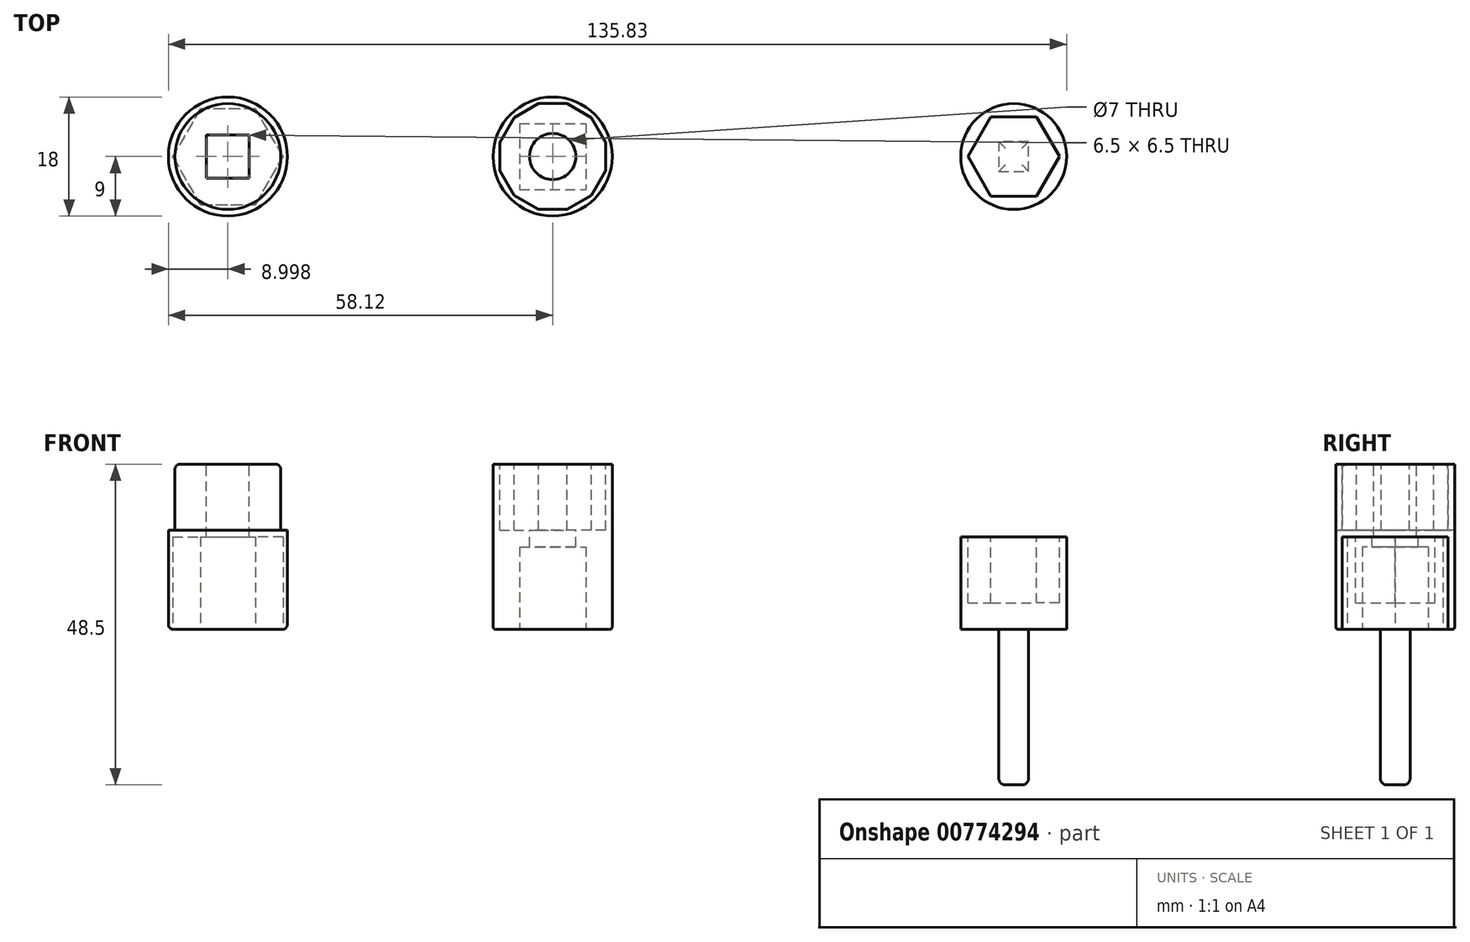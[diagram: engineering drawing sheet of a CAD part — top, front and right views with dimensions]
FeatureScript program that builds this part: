
annotation { "Feature Type Name" : "Feature", "Feature Type Description" : "" }
export const myFeature = defineFeature(function(context is Context, id is Id, definition is map)
    precondition{}
    {
        {
            var Q0;
            Q0=qCreatedBy(makeId("Top.planeOp"),FACE);
            var sketch = newSketch(context, id + "F0", { "sketchPlane" : qUnion([Q0])});
            skCircle(sketch, "E0", {"center": v(0, 0) * mm, "radius": 9 * mm});
            skLineSegment(sketch, "E1.bottom", {"start": v(-5, 5) * mm, "end": v(5, 5) * mm});
            skLineSegment(sketch, "E1.top", {"start": v(-5, -5) * mm, "end": v(5, -5) * mm});
            skLineSegment(sketch, "E1.left", {"start": v(-5, 5) * mm, "end": v(-5, -5) * mm});
            skLineSegment(sketch, "E1.right", {"start": v(5, 5) * mm, "end": v(5, -5) * mm});
            skSolve(sketch);
        }
        {
            var Q0;
            Q0=makeQuery(id+"F0.imprint","IMPRINT",FACE,{"disambiguationData":[TD([[makeQuery(id+"F0.imprint","IMPRINT",EDGE,{"derivedFrom":sQuery(id+"F0.wireOp",EDGE,"E0")}),1.0]])]});
            var Q1;
            {var subQ1=sQuery(id+"F0.wireOp",EDGE,"03wSvE2e-Fg7S-AAcF-NH9x-LQPhPzigft5H.right");var subQ6=sQuery(id+"F0.wireOp",EDGE,"03wSvE2e-Fg7S-AAcF-NH9x-LQPhPzigft5H.bottom");var subQ9=makeQuery(id+"F0.imprint","INTERSECT",VERTEX,{"derivedFrom":[subQ6,subQ1]});Q1=makeQuery(id+"F0.imprint","IMPRINT",FACE,{"disambiguationData":[TD([[makeQuery(id+"F0.imprint","IMPRINT",EDGE,{"disambiguationData":[TD([[subQ9,1.0]])],"derivedFrom":subQ6}),-1.0]])]});}
            var Q2;
            {var subQ1=sQuery(id+"F0.wireOp",EDGE,"03wSvE2e-Fg7S-AAcF-NH9x-LQPhPzigft5H.right");var subQ6=sQuery(id+"F0.wireOp",EDGE,"03wSvE2e-Fg7S-AAcF-NH9x-LQPhPzigft5H.top");var subQ9=makeQuery(id+"F0.imprint","INTERSECT",VERTEX,{"derivedFrom":[subQ6,subQ1]});Q2=makeQuery(id+"F0.imprint","IMPRINT",FACE,{"disambiguationData":[TD([[makeQuery(id+"F0.imprint","IMPRINT",EDGE,{"disambiguationData":[TD([[subQ9,1.0]])],"derivedFrom":subQ6}),1.0]])]});}
            var Q3;
            {var subQ1=sQuery(id+"F0.wireOp",EDGE,"03wSvE2e-Fg7S-AAcF-NH9x-LQPhPzigft5H.top");var subQ5=sQuery(id+"F0.wireOp",EDGE,"03wSvE2e-Fg7S-AAcF-NH9x-LQPhPzigft5H.left");var subQ6=makeQuery(id+"F0.imprint","INTERSECT",VERTEX,{"derivedFrom":[subQ1,subQ5]});Q3=makeQuery(id+"F0.imprint","IMPRINT",FACE,{"disambiguationData":[TD([[makeQuery(id+"F0.imprint","IMPRINT",EDGE,{"disambiguationData":[TD([[subQ6,-1.0]])],"derivedFrom":subQ1}),1.0]])]});}
            var Q4;
            {var subQ1=sQuery(id+"F0.wireOp",EDGE,"03wSvE2e-Fg7S-AAcF-NH9x-LQPhPzigft5H.left");var subQ6=sQuery(id+"F0.wireOp",EDGE,"03wSvE2e-Fg7S-AAcF-NH9x-LQPhPzigft5H.bottom");var subQ9=makeQuery(id+"F0.imprint","INTERSECT",VERTEX,{"derivedFrom":[subQ6,subQ1]});Q4=makeQuery(id+"F0.imprint","IMPRINT",FACE,{"disambiguationData":[TD([[makeQuery(id+"F0.imprint","IMPRINT",EDGE,{"disambiguationData":[TD([[subQ9,-1.0]])],"derivedFrom":subQ6}),-1.0]])]});}
            var Q5;
            {var subQ0=sQuery(id+"F0.wireOp",EDGE,"0nZERG67-7UOP-U3bg-9f60-7EF7LwZAKck1");var subQ1=sQuery(id+"F0.wireOp",EDGE,"W0zUS9TI-iheG-UtfQ-mQPj-YblpC81evcvk");var subQ2=makeQuery(id+"F0.imprint","INTERSECT",VERTEX,{"disambiguationData":[OD(0.0)],"derivedFrom":[subQ1,subQ0]});Q5=makeQuery(id+"F0.imprint","IMPRINT",FACE,{"disambiguationData":[TD([[makeQuery(id+"F0.imprint","IMPRINT",EDGE,{"disambiguationData":[TD([[subQ2,-1.0]])],"derivedFrom":subQ1}),-1.0]])]});}
            var Q6;
            {var subQ0=sQuery(id+"F0.wireOp",EDGE,"zQuLa7GF-zexE-TRTW-qUjA-5ZPmynHRBfk2");var subQ1=sQuery(id+"F0.wireOp",EDGE,"W0zUS9TI-iheG-UtfQ-mQPj-YblpC81evcvk");var subQ2=makeQuery(id+"F0.imprint","INTERSECT",VERTEX,{"derivedFrom":[subQ1,subQ0]});Q6=makeQuery(id+"F0.imprint","IMPRINT",FACE,{"disambiguationData":[TD([[makeQuery(id+"F0.imprint","IMPRINT",EDGE,{"disambiguationData":[TD([[subQ2,-1.0]])],"derivedFrom":subQ1}),1.0]])]});}
            var Q7;
            {var subQ0=sQuery(id+"F0.wireOp",EDGE,"zQuLa7GF-zexE-TRTW-qUjA-5ZPmynHRBfk2");var subQ1=sQuery(id+"F0.wireOp",EDGE,"W0zUS9TI-iheG-UtfQ-mQPj-YblpC81evcvk");var subQ2=makeQuery(id+"F0.imprint","INTERSECT",VERTEX,{"derivedFrom":[subQ1,subQ0]});Q7=makeQuery(id+"F0.imprint","IMPRINT",FACE,{"disambiguationData":[TD([[makeQuery(id+"F0.imprint","IMPRINT",EDGE,{"disambiguationData":[TD([[subQ2,-1.0]])],"derivedFrom":subQ1}),-1.0]])]});}
            var Q8;
            {var subQ0=sQuery(id+"F0.wireOp",EDGE,"0nZERG67-7UOP-U3bg-9f60-7EF7LwZAKck1");var subQ1=sQuery(id+"F0.wireOp",EDGE,"W0zUS9TI-iheG-UtfQ-mQPj-YblpC81evcvk");var subQ2=makeQuery(id+"F0.imprint","INTERSECT",VERTEX,{"disambiguationData":[OD(0.0)],"derivedFrom":[subQ1,subQ0]});Q8=makeQuery(id+"F0.imprint","IMPRINT",FACE,{"disambiguationData":[TD([[makeQuery(id+"F0.imprint","IMPRINT",EDGE,{"disambiguationData":[TD([[subQ2,-1.0]])],"derivedFrom":subQ1}),1.0]])]});}
            extrude(context, id + "F1", {"entities" : qUnion([Q0, Q1, Q2, Q3, Q4, Q5, Q6, Q7, Q8]), "depth" : 12.5 * mm, "offsetDistance" : 25 * mm});
        }
        {
            var Q0;
            Q0=makeQuery(id+"F1.opExtrude","CAP_EDGE",EDGE,{"disambiguationData":[OSD([sQuery(id+"F0.wireOp",EDGE,"E0")])],"isStart":true});
            fillet(context, id + "F2", {"entities" : qUnion([Q0]), "radius" : .4 * mm, "tangentPropagation" : true, "allowEdgeOverflow" : false});
        }
        {
            var Q0;
            Q0=makeQuery(id+"F1.opExtrude","CAP_FACE",FACE,{"disambiguationData":[OSD([sQuery(id+"F0.wireOp",EDGE,"E0")])],"isStart":false});
            var sketch = newSketch(context, id + "F3", { "sketchPlane" : qUnion([Q0])});
            skCircle(sketch, "E2", {"center": v(0, 0) * mm, "radius": 9 * mm});
            skSolve(sketch);
        }
        {
            var Q0;
            Q0 = qSketchRegion(id + "F3", true);
            extrude(context, id + "F4", {"entities" : qUnion([Q0]), "operationType" : NewBodyOperationType.ADD, "depth" : 12.5 * mm, "offsetDistance" : 25 * mm});
        }
        {
            var Q0;
            Q0=makeQuery(id+"F4.opExtrude","CAP_FACE",FACE,{"disambiguationData":[OSD([sQuery(id+"F3.wireOp",EDGE,"E2")])],"isStart":false});
            var sketch = newSketch(context, id + "F5", { "sketchPlane" : qUnion([Q0])});
            skCircle(sketch, "E3.cCircle", {"center": v(0, 0) * mm, "radius": 8 * mm, "construction": true});
            skLineSegment(sketch, "E3.0", {"start": v(-2.14, 8) * mm, "end": v(2.14, 8) * mm});
            skLineSegment(sketch, "E3.1", {"start": v(2.14, 8) * mm, "end": v(5.86, 5.86) * mm});
            skLineSegment(sketch, "E3.2", {"start": v(5.86, 5.86) * mm, "end": v(8, 2.14) * mm});
            skLineSegment(sketch, "E3.3", {"start": v(8, 2.14) * mm, "end": v(8, -2.14) * mm});
            skLineSegment(sketch, "E3.4", {"start": v(8, -2.14) * mm, "end": v(5.86, -5.86) * mm});
            skLineSegment(sketch, "E3.5", {"start": v(5.86, -5.86) * mm, "end": v(2.14, -8) * mm});
            skLineSegment(sketch, "E3.6", {"start": v(2.14, -8) * mm, "end": v(-2.14, -8) * mm});
            skLineSegment(sketch, "E3.7", {"start": v(-2.14, -8) * mm, "end": v(-5.86, -5.86) * mm});
            skLineSegment(sketch, "E3.8", {"start": v(-5.86, -5.86) * mm, "end": v(-8, -2.14) * mm});
            skLineSegment(sketch, "E3.9", {"start": v(-8, -2.14) * mm, "end": v(-8, 2.14) * mm});
            skLineSegment(sketch, "E3.10", {"start": v(-8, 2.14) * mm, "end": v(-5.86, 5.86) * mm});
            skLineSegment(sketch, "E3.11", {"start": v(-5.86, 5.86) * mm, "end": v(-2.14, 8) * mm});
            skPoint(sketch, "E3.0.midPoint", {"position": v(0, 8) * mm});
            skSolve(sketch);
        }
        {
            var Q0;
            Q0 = qSketchRegion(id + "F5", true);
            extrude(context, id + "F6", {"entities" : qUnion([Q0]), "operationType" : NewBodyOperationType.REMOVE, "oppositeDirection" : true, "depth" : 10 * mm, "offsetDistance" : 25 * mm});
        }
        {
            var Q0;
            Q0=qCreatedBy(makeId("Top.planeOp"),FACE);
            var sketch = newSketch(context, id + "F7", { "sketchPlane" : qUnion([Q0])});
            skCircle(sketch, "E4", {"center": v(69.71, 0) * mm, "radius": 8 * mm});
            skSolve(sketch);
        }
        {
            var Q0;
            Q0 = qSketchRegion(id + "F7", true);
            extrude(context, id + "F8", {"entities" : qUnion([Q0]), "depth" : 14 * mm, "offsetDistance" : 25 * mm});
        }
        {
            var Q0;
            Q0=makeQuery(id+"F8.opExtrude","CAP_FACE",FACE,{"disambiguationData":[OSD([sQuery(id+"F7.wireOp",EDGE,"E4")])],"isStart":true});
            var sketch = newSketch(context, id + "F9", { "sketchPlane" : qUnion([Q0])});
            skCircle(sketch, "E5.cCircle", {"center": v(69.71, 0) * mm, "radius": 2.25 * mm});
            skLineSegment(sketch, "E5.0", {"start": v(67.46, 2.25) * mm, "end": v(71.96, 2.25) * mm});
            skLineSegment(sketch, "E5.1", {"start": v(71.96, 2.25) * mm, "end": v(71.96, -2.25) * mm});
            skLineSegment(sketch, "E5.2", {"start": v(71.96, -2.25) * mm, "end": v(67.46, -2.25) * mm});
            skLineSegment(sketch, "E5.3", {"start": v(67.46, -2.25) * mm, "end": v(67.46, 2.25) * mm});
            skPoint(sketch, "E5.0.midPoint", {"position": v(69.71, 2.25) * mm});
            skSolve(sketch);
        }
        {
            var Q0;
            {var subQ0=sQuery(id+"F9.wireOp",EDGE,"E5.1");var subQ1=sQuery(id+"F9.wireOp",EDGE,"E5.cCircle");var subQ2=makeQuery(id+"F9.imprint","INTERSECT",VERTEX,{"derivedFrom":[subQ1,subQ0]});Q0=makeQuery(id+"F9.imprint","IMPRINT",FACE,{"disambiguationData":[TD([[makeQuery(id+"F9.imprint","IMPRINT",EDGE,{"disambiguationData":[TD([[subQ2,1.0]])],"derivedFrom":subQ1}),-1.0]])]});}
            var Q1;
            {var subQ0=sQuery(id+"F9.wireOp",EDGE,"E5.0");var subQ1=sQuery(id+"F9.wireOp",EDGE,"E5.cCircle");var subQ2=makeQuery(id+"F9.imprint","INTERSECT",VERTEX,{"derivedFrom":[subQ1,subQ0]});Q1=makeQuery(id+"F9.imprint","IMPRINT",FACE,{"disambiguationData":[TD([[makeQuery(id+"F9.imprint","IMPRINT",EDGE,{"disambiguationData":[TD([[subQ2,1.0]])],"derivedFrom":subQ1}),-1.0]])]});}
            var Q2;
            {var subQ0=sQuery(id+"F9.wireOp",EDGE,"E5.3");var subQ1=sQuery(id+"F9.wireOp",EDGE,"E5.cCircle");var subQ2=makeQuery(id+"F9.imprint","INTERSECT",VERTEX,{"derivedFrom":[subQ1,subQ0]});Q2=makeQuery(id+"F9.imprint","IMPRINT",FACE,{"disambiguationData":[TD([[makeQuery(id+"F9.imprint","IMPRINT",EDGE,{"disambiguationData":[TD([[subQ2,-1.0]])],"derivedFrom":subQ1}),-1.0]])]});}
            var Q3;
            {var subQ0=sQuery(id+"F9.wireOp",EDGE,"E5.cCircle");var subQ1=makeQuery(id+"F9.imprint","INTERSECT",VERTEX,{"derivedFrom":[subQ0,sQuery(id+"F9.wireOp",EDGE,"E5.0")]});Q3=makeQuery(id+"F9.imprint","IMPRINT",FACE,{"disambiguationData":[TD([[makeQuery(id+"F9.imprint","IMPRINT",EDGE,{"disambiguationData":[TD([[subQ1,1.0]])],"derivedFrom":subQ0}),1.0]])]});}
            var Q4;
            {var subQ0=sQuery(id+"F9.wireOp",EDGE,"E5.0");var subQ1=sQuery(id+"F9.wireOp",EDGE,"E5.cCircle");var subQ2=makeQuery(id+"F9.imprint","INTERSECT",VERTEX,{"derivedFrom":[subQ1,subQ0]});Q4=makeQuery(id+"F9.imprint","IMPRINT",FACE,{"disambiguationData":[TD([[makeQuery(id+"F9.imprint","IMPRINT",EDGE,{"disambiguationData":[TD([[subQ2,-1.0]])],"derivedFrom":subQ1}),-1.0]])]});}
            extrude(context, id + "F10", {"entities" : qUnion([Q0, Q1, Q2, Q3, Q4]), "operationType" : NewBodyOperationType.ADD, "depth" : 23.5 * mm, "offsetDistance" : 25 * mm});
        }
        {
            var Q0;
            Q0=makeQuery(id+"F6.boolean.opBoolean","COPY",FACE,{"derivedFrom":makeQuery(id+"F6.opExtrude","CAP_FACE",FACE,{"disambiguationData":[OSD([sQuery(id+"F5.wireOp",EDGE,"E3.0"),sQuery(id+"F5.wireOp",EDGE,"E3.1"),sQuery(id+"F5.wireOp",EDGE,"E3.2"),sQuery(id+"F5.wireOp",EDGE,"E3.3"),sQuery(id+"F5.wireOp",EDGE,"E3.4"),sQuery(id+"F5.wireOp",EDGE,"E3.5"),sQuery(id+"F5.wireOp",EDGE,"E3.6"),sQuery(id+"F5.wireOp",EDGE,"E3.7"),sQuery(id+"F5.wireOp",EDGE,"E3.8"),sQuery(id+"F5.wireOp",EDGE,"E3.9"),sQuery(id+"F5.wireOp",EDGE,"E3.10"),sQuery(id+"F5.wireOp",EDGE,"E3.11")])],"isStart":false})});
            var sketch = newSketch(context, id + "F11", { "sketchPlane" : qUnion([Q0])});
            skCircle(sketch, "E6", {"center": v(0, 0) * mm, "radius": 3.5 * mm});
            skSolve(sketch);
        }
        {
            var Q0;
            Q0 = qSketchRegion(id + "F11", true);
            extrude(context, id + "F12", {"entities" : qUnion([Q0]), "operationType" : NewBodyOperationType.REMOVE, "oppositeDirection" : true, "depth" : 12 * mm, "offsetDistance" : 25 * mm});
        }
        {
            var Q0;
            Q0=makeQuery(id+"F10.opExtrude","CAP_EDGE",EDGE,{"disambiguationData":[OSD([sQuery(id+"F9.wireOp",EDGE,"E5.2")])],"isStart":false});
            var Q1;
            Q1=makeQuery(id+"F10.opExtrude","CAP_EDGE",EDGE,{"disambiguationData":[OSD([sQuery(id+"F9.wireOp",EDGE,"E5.1")])],"isStart":false});
            var Q2;
            Q2=makeQuery(id+"F10.opExtrude","CAP_EDGE",EDGE,{"disambiguationData":[OSD([sQuery(id+"F9.wireOp",EDGE,"E5.0")])],"isStart":false});
            var Q3;
            Q3=makeQuery(id+"F10.opExtrude","CAP_EDGE",EDGE,{"disambiguationData":[OSD([sQuery(id+"F9.wireOp",EDGE,"E5.3")])],"isStart":false});
            fillet(context, id + "F13", {"entities" : qUnion([Q0, Q1, Q2, Q3]), "radius" : 1 * mm, "tangentPropagation" : true, "allowEdgeOverflow" : false});
        }
        {
            var Q0;
            Q0=qCreatedBy(makeId("Top.planeOp"),FACE);
            var sketch = newSketch(context, id + "F14", { "sketchPlane" : qUnion([Q0])});
            skCircle(sketch, "E7", {"center": v(-49.12, 0) * mm, "radius": 9 * mm});
            skSolve(sketch);
        }
        {
            var Q0;
            Q0 = qSketchRegion(id + "F14", true);
            extrude(context, id + "F15", {"entities" : qUnion([Q0]), "depth" : 15 * mm, "offsetDistance" : 25 * mm});
        }
        {
            var Q0;
            Q0=makeQuery(id+"F15.opExtrude","CAP_FACE",FACE,{"disambiguationData":[OSD([sQuery(id+"F14.wireOp",EDGE,"E7"),sQuery(id+"F14.wireOp",EDGE,"6d6a7b4d-6cfd-47b6-aa00-b523f6408a61.0"),sQuery(id+"F14.wireOp",EDGE,"6d6a7b4d-6cfd-47b6-aa00-b523f6408a61.1"),sQuery(id+"F14.wireOp",EDGE,"6d6a7b4d-6cfd-47b6-aa00-b523f6408a61.2"),sQuery(id+"F14.wireOp",EDGE,"6d6a7b4d-6cfd-47b6-aa00-b523f6408a61.3"),sQuery(id+"F14.wireOp",EDGE,"6d6a7b4d-6cfd-47b6-aa00-b523f6408a61.4"),sQuery(id+"F14.wireOp",EDGE,"6d6a7b4d-6cfd-47b6-aa00-b523f6408a61.5")])],"isStart":false});
            var sketch = newSketch(context, id + "F16", { "sketchPlane" : qUnion([Q0])});
            skCircle(sketch, "E8", {"center": v(-49.12, 0) * mm, "radius": 8 * mm});
            skSolve(sketch);
        }
        {
            var Q0;
            Q0 = qSketchRegion(id + "F16", true);
            extrude(context, id + "F17", {"entities" : qUnion([Q0]), "operationType" : NewBodyOperationType.ADD, "depth" : 10 * mm, "offsetDistance" : 25 * mm});
        }
        {
            var Q0;
            Q0=makeQuery(id+"F15.opExtrude","CAP_FACE",FACE,{"disambiguationData":[OSD([sQuery(id+"F14.wireOp",EDGE,"E7")])],"isStart":true});
            var sketch = newSketch(context, id + "F18", { "sketchPlane" : qUnion([Q0])});
            skLineSegment(sketch, "E9.0", {"start": v(-53.29, 7.26) * mm, "end": v(-44.94, 7.26) * mm});
            skLineSegment(sketch, "E9.1", {"start": v(-44.94, 7.26) * mm, "end": v(-40.77, 0.03) * mm});
            skLineSegment(sketch, "E9.2", {"start": v(-40.77, 0.03) * mm, "end": v(-44.94, -7.2) * mm});
            skLineSegment(sketch, "E9.3", {"start": v(-44.94, -7.2) * mm, "end": v(-53.29, -7.2) * mm});
            skLineSegment(sketch, "E9.4", {"start": v(-53.29, -7.2) * mm, "end": v(-57.46, 0.03) * mm});
            skLineSegment(sketch, "E9.5", {"start": v(-57.46, 0.03) * mm, "end": v(-53.29, 7.26) * mm});
            skSolve(sketch);
        }
        {
            var Q0;
            Q0=makeQuery(id+"F18.imprint","IMPRINT",FACE,{"disambiguationData":[TD([[makeQuery(id+"F18.imprint","IMPRINT",EDGE,{"derivedFrom":sQuery(id+"F18.wireOp",EDGE,"E9.0")}),-1.0]])]});
            extrude(context, id + "F19", {"entities" : qUnion([Q0]), "operationType" : NewBodyOperationType.REMOVE, "oppositeDirection" : true, "depth" : 14 * mm, "offsetDistance" : 25 * mm});
        }
        {
            var Q0;
            Q0=makeQuery(id+"F17.opExtrude","CAP_FACE",FACE,{"disambiguationData":[OSD([sQuery(id+"F16.wireOp",EDGE,"E8")])],"isStart":false});
            var sketch = newSketch(context, id + "F20", { "sketchPlane" : qUnion([Q0])});
            skLineSegment(sketch, "E10.bottom", {"start": v(-45.87, -3.25) * mm, "end": v(-52.37, -3.25) * mm});
            skLineSegment(sketch, "E10.top", {"start": v(-45.87, 3.25) * mm, "end": v(-52.37, 3.25) * mm});
            skLineSegment(sketch, "E10.left", {"start": v(-45.87, -3.25) * mm, "end": v(-45.87, 3.25) * mm});
            skLineSegment(sketch, "E10.right", {"start": v(-52.37, -3.25) * mm, "end": v(-52.37, 3.25) * mm});
            skSolve(sketch);
        }
        {
            var Q0;
            Q0 = qSketchRegion(id + "F20", true);
            extrude(context, id + "F21", {"entities" : qUnion([Q0]), "operationType" : NewBodyOperationType.REMOVE, "oppositeDirection" : true, "depth" : 25 * mm, "offsetDistance" : 25 * mm});
        }
        {
            var Q0;
            Q0=makeQuery(id+"F17.opExtrude","CAP_EDGE",EDGE,{"disambiguationData":[OSD([sQuery(id+"F16.wireOp",EDGE,"E8")])],"isStart":false});
            var Q1;
            Q1=makeQuery(id+"F15.opExtrude","CAP_EDGE",EDGE,{"disambiguationData":[OSD([sQuery(id+"F14.wireOp",EDGE,"E7")])],"isStart":true});
            fillet(context, id + "F22", {"entities" : qUnion([Q0, Q1]), "radius" : .8 * mm, "tangentPropagation" : true, "allowEdgeOverflow" : false});
        }
        {
            var Q0;
            Q0=makeQuery(id+"F8.opExtrude","CAP_FACE",FACE,{"disambiguationData":[OSD([sQuery(id+"F7.wireOp",EDGE,"E4")])],"isStart":false});
            var sketch = newSketch(context, id + "F23", { "sketchPlane" : qUnion([Q0])});
            skLineSegment(sketch, "E11.0", {"start": v(66.25, 6) * mm, "end": v(73.18, 6) * mm});
            skLineSegment(sketch, "E11.1", {"start": v(73.18, 6) * mm, "end": v(76.64, 0) * mm});
            skLineSegment(sketch, "E11.2", {"start": v(76.64, 0) * mm, "end": v(73.18, -6) * mm});
            skLineSegment(sketch, "E11.3", {"start": v(73.18, -6) * mm, "end": v(66.25, -6) * mm});
            skLineSegment(sketch, "E11.4", {"start": v(66.25, -6) * mm, "end": v(62.78, 0) * mm});
            skLineSegment(sketch, "E11.5", {"start": v(62.78, 0) * mm, "end": v(66.25, 6) * mm});
            skPoint(sketch, "E11.0.midPoint", {"position": v(69.71, 6) * mm});
            skSolve(sketch);
        }
        {
            var Q0;
            Q0=makeQuery(id+"F23.imprint","IMPRINT",FACE,{"disambiguationData":[TD([[makeQuery(id+"F23.imprint","IMPRINT",EDGE,{"derivedFrom":sQuery(id+"F23.wireOp",EDGE,"E11.0")}),-1.0]])]});
            extrude(context, id + "F24", {"entities" : qUnion([Q0]), "operationType" : NewBodyOperationType.REMOVE, "oppositeDirection" : true, "depth" : 10 * mm, "offsetDistance" : 25 * mm});
        }
    });
